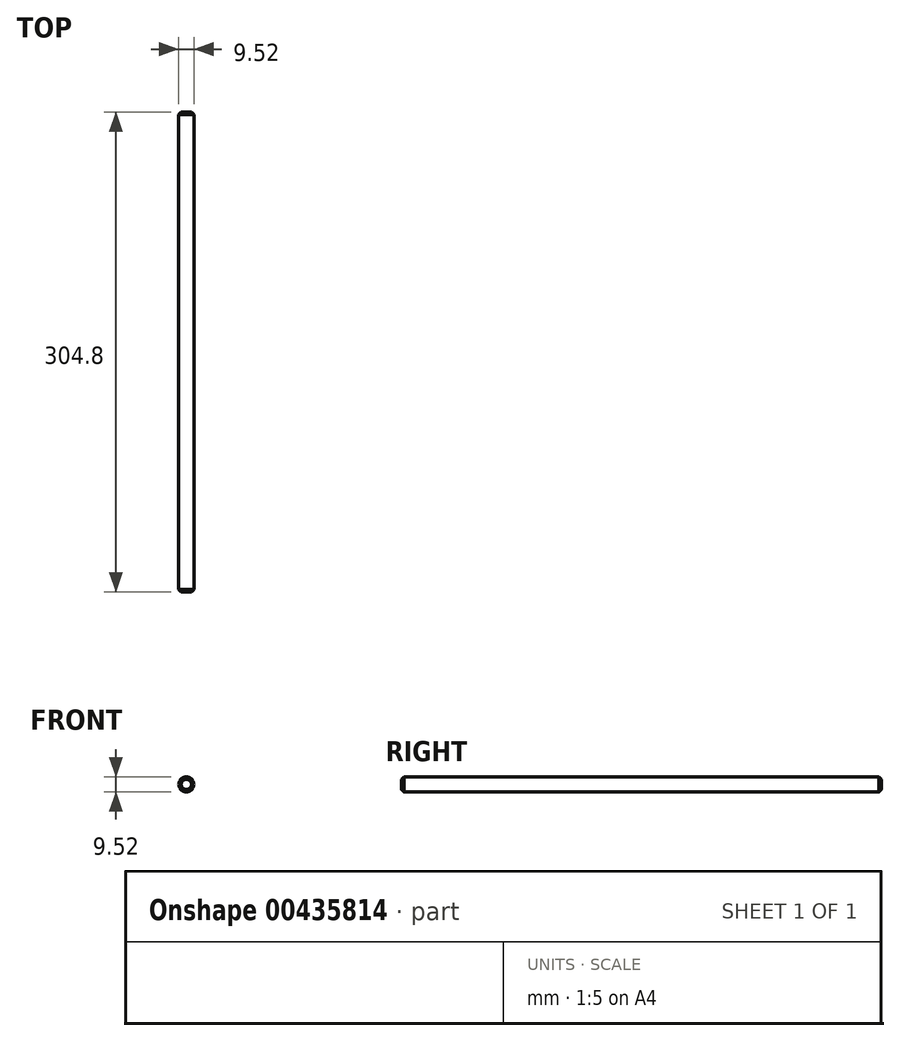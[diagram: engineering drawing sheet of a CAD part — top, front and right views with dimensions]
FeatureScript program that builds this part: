
annotation { "Feature Type Name" : "Feature", "Feature Type Description" : "" }
export const myFeature = defineFeature(function(context is Context, id is Id, definition is map)
    precondition{}
    {
        {
            var Q0;
            Q0=qCreatedBy(makeId("Front.planeOp"),FACE);
            var sketch = newSketch(context, id + "F0", { "sketchPlane" : qUnion([Q0])});
            skCircle(sketch, "E0", {"center": v(0, 0) * mm, "radius": 4.76 * mm});
            skSolve(sketch);
        }
        {
            var Q0;
            Q0=makeQuery(id+"F0.imprint","IMPRINT",FACE,{"disambiguationData":[TD([[makeQuery(id+"F0.imprint","IMPRINT",EDGE,{"derivedFrom":sQuery(id+"F0.wireOp",EDGE,"E0")}),1.0]])]});
            extrude(context, id + "F1", {"entities" : qUnion([Q0]), "endBound" : BoundingType.SYMMETRIC, "depth" : 304.8 * mm});
        }
        {
            var Q0;
            Q0=makeQuery(id+"F1.opExtrude","CAP_EDGE",EDGE,{"disambiguationData":[OSD([sQuery(id+"F0.wireOp",EDGE,"E0")])],"isStart":false});
            var Q1;
            Q1=makeQuery(id+"F1.opExtrude","SWEPT_FACE",FACE,{"disambiguationData":[OSD([sQuery(id+"F0.wireOp",EDGE,"E0")])]});
            chamfer(context, id + "F2", {"entities" : qUnion([Q0, Q1]), "width" : 1.52 * mm, "tangentPropagation" : true});
        }
    });
